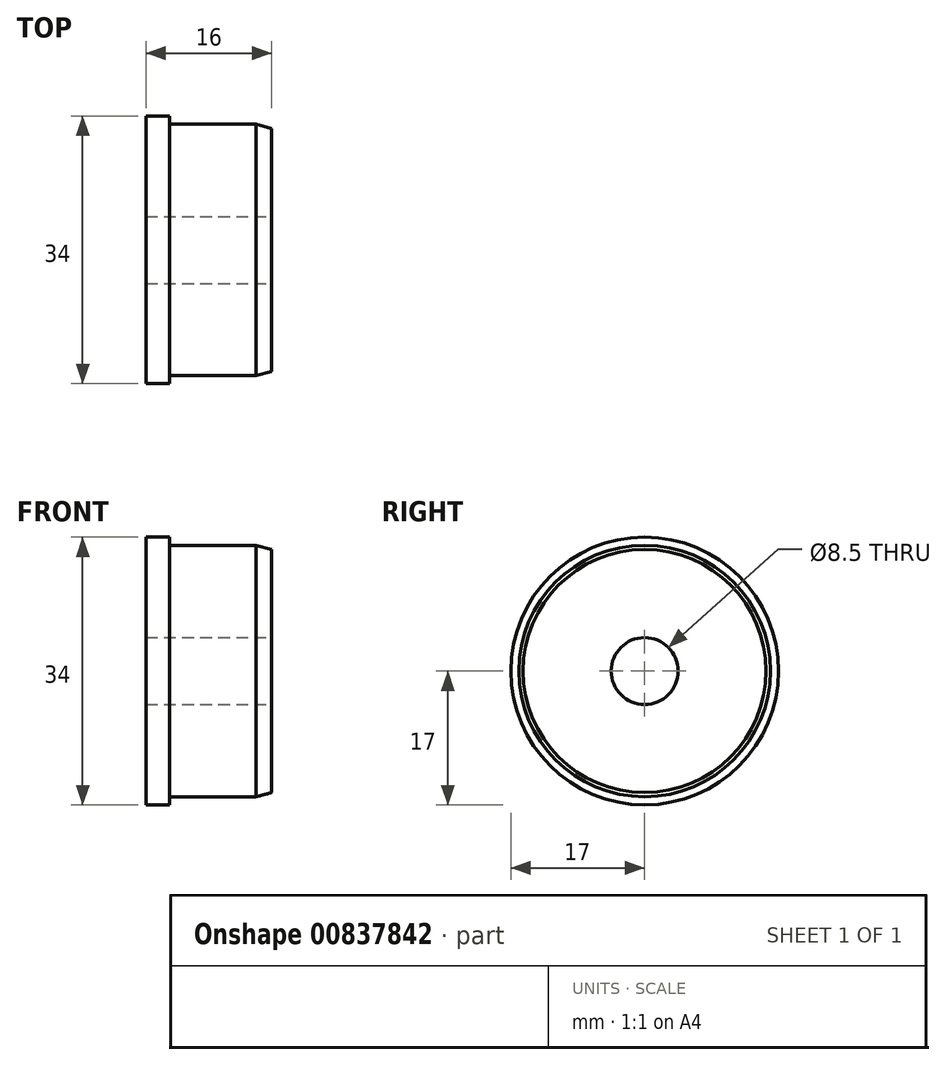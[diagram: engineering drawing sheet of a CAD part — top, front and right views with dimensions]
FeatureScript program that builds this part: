
annotation { "Feature Type Name" : "Feature", "Feature Type Description" : "" }
export const myFeature = defineFeature(function(context is Context, id is Id, definition is map)
    precondition{}
    {
        {
            var Q0;
            Q0=qCreatedBy(makeId("Front.planeOp"),FACE);
            var sketch = newSketch(context, id + "F0", { "sketchPlane" : qUnion([Q0])});
            skLineSegment(sketch, "E0", {"start": v(0, 0) * mm, "end": v(0, 17) * mm});
            skLineSegment(sketch, "E1", {"start": v(0, 17) * mm, "end": v(3, 17) * mm});
            skLineSegment(sketch, "E2", {"start": v(3, 17) * mm, "end": v(3, 15.97) * mm});
            skLineSegment(sketch, "E3", {"start": v(3, 15.97) * mm, "end": v(16, 15.97) * mm});
            skLineSegment(sketch, "E4", {"start": v(16, 15.97) * mm, "end": v(16, 0) * mm});
            skLineSegment(sketch, "E5", {"start": v(0, 0) * mm, "end": v(16, 0) * mm});
            skSolve(sketch);
        }
        {
            var Q0;
            Q0=makeQuery(id+"F0.imprint","IMPRINT",FACE,{"disambiguationData":[TD([[makeQuery(id+"F0.imprint","IMPRINT",EDGE,{"derivedFrom":sQuery(id+"F0.wireOp",EDGE,"E0")}),-1.0]])]});
            var Q1;
            Q1=sQuery(id+"F0.wireOp",EDGE,"E5");
            revolve(context, id + "F1", {"surfaceOperationType" : NewSurfaceOperationType.NEW, "entities" : qUnion([Q0]), "axis" : qUnion([Q1]), "revolveType" : RevolveType.FULL});
        }
        {
            var Q0;
            Q0=makeQuery(id+"F1.opRevolve","SWEPT_FACE",FACE,{"disambiguationData":[OSD([sQuery(id+"F0.wireOp",EDGE,"E4")])]});
            var sketch = newSketch(context, id + "F2", { "sketchPlane" : qUnion([Q0])});
            skPoint(sketch, "E6.0", {"position": v(0, 0) * mm});
            skSolve(sketch);
        }
        {
            var Q0;
            Q0=sQuery(id+"F2.wireOp",VERTEX,"E6.0");
            var Q1;
            Q1=makeQuery(id+"F1.opRevolve","SWEPT_BODY",BODY,{"disambiguationData":[OSD([sQuery(id+"F0.wireOp",EDGE,"E0"),sQuery(id+"F0.wireOp",EDGE,"E1"),sQuery(id+"F0.wireOp",EDGE,"E2"),sQuery(id+"F0.wireOp",EDGE,"E3"),sQuery(id+"F0.wireOp",EDGE,"E4"),sQuery(id+"F0.wireOp",EDGE,"E5")])]});
            hole(context, id + "F3", {"style" : HoleStyle.SIMPLE, "endStyle" : HoleEndStyle.THROUGH, "standardTappedOrClearance" : lookupTablePath({ "standard" : "ISO", "engagement" : "75%", "pitch" : "1.5 mm", "size" : "M10", "type" : "Tapped" }), "standardBlindInLast" : lookupTablePath({ "standard" : "ISO", "engagement" : "75%", "pitch" : "1.5 mm", "size" : "M10", "type" : "Tapped" }), "holeDiameter" : 8.5 * mm, "majorDiameter" : 10 * mm, "showTappedDepth" : true, "isTappedThrough" : true, "tappedDepth" : 12 * mm, "tapClearance" : 3, "locations" : qUnion([Q0]), "scope" : qUnion([Q1])});
        }
        {
            var Q0;
            Q0=makeQuery(id+"F1.opRevolve","SWEPT_EDGE",EDGE,{"disambiguationData":[OSD([sQuery(id+"F0.wireOp",EDGE,"E3"),sQuery(id+"F0.wireOp",EDGE,"E4")])]});
            chamfer(context, id + "F4", {"entities" : qUnion([Q0]), "chamferType" : ChamferType.OFFSET_ANGLE, "width" : 2 * mm, "oppositeDirection" : false, "angle" : 15 * degree, "tangentPropagation" : true});
        }
    });
